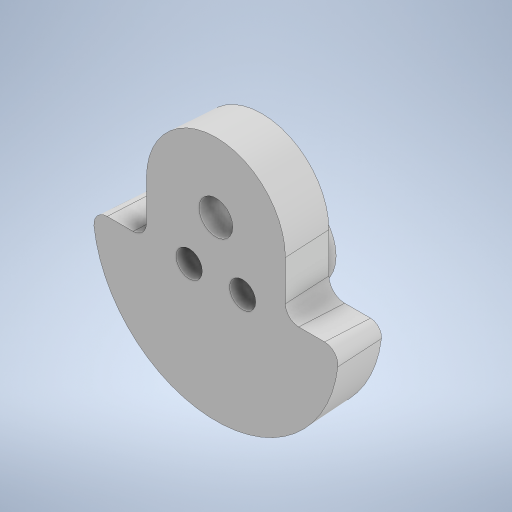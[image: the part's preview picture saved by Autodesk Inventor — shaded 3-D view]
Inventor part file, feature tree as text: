
AUTODESK INVENTOR PART (.ipt)
format: ipt  version: 2023 (Build 270158000, 158)  size: 496,640 bytes
history: native  units: in
note: dims shown in document units (in); Inventor stores cm internally (conversion verified against a paired STEP export)
features: extrude x5, draft x2, sketch x1, fillet x1
ambient origin geometry x8: Origin, YZ Plane, XZ Plane, XY Plane, X Axis, Y Axis, Z Axis, Center Point
bodies: Body1 (feature_tree)
feature tree (9):
  sketch  "Sketch1"  dims[d3=0.866in d15=0.75in d20=0.316in d37=0.75in d44=0.125in d52=0.245in d57=0.74in d58=0.75in d59=0.0in d60=0.32in d61=0.0in d62=1.5in d63=0.0in d64=1.5in d65=0.0in d66=0.375in d67=0.0in d68=0.125in d70=0.135in d71=0.0206in d72=0.0412in d73=1.15in]
  extrude  "Extrusion9"  Depth=0.125in
  extrude  "Extrusion10"  Depth=0.125in
  extrude  "Extrusion11"  Depth=0.125in
  extrude  "Extrusion12"  Depth=0.125in
  extrude  "Extrusion13"  Depth=0.125in
  fillet  "Fillet2"  Radius=0.75in
  draft  "FaceDraft1"
  draft  "FaceDraft2"
